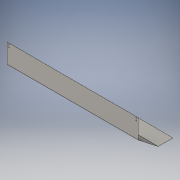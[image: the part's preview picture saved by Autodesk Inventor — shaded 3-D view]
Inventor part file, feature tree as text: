
AUTODESK INVENTOR PART (.ipt)
format: ipt  version: 2016 (Build 200138000, 138)  size: 175,616 bytes
history: native  units: mm
features: sheet_metal_op x7, sketch x4, other x4, hole x1
ambient origin geometry x8: Origin, YZ Plane, XZ Plane, XY Plane, X Axis, Y Axis, Z Axis, Center Point
bodies: Solid1 (feature_tree)
feature tree (16):
  sheet_metal_op  "Face1"
  sheet_metal_op  "Flange1"
  sheet_metal_op  "Flange2"
  hole  "Hole1"  [1 undecoded]
  sketch  "Sketch1"  dims[d0=190.0mm d1=1695.0mm]
  other  "Plate1"
  sketch  "Sketch2"  dims[d2=1.6mm]
  other  "Plate2"
  sheet_metal_op  "Bend1"
  sheet_metal_op  "Corner1"
  sketch  "Sketch3"  dims[d3=1.6mm]
  other  "Plate3"
  sheet_metal_op  "Bend2"
  sheet_metal_op  "Corner2"
  sketch  "Sketch4"  dims[d4=0.8mm d5=3.2mm d6=1.6mm d7=330.0mm d8=6.632251mm d9=1.6mm d10=6.4mm d11=1.6mm d12=1.6mm d13=1.6mm d14=0.8mm d15=3.2mm d16=1.6mm d17=250.0mm d18=9.075712mm d19=1.6mm d20=6.4mm d21=1.6mm d22=1.6mm d23=60.0mm d24=12.0mm d25=12.0mm d26=25.0mm d27=25.0mm d28=15.0mm d29=15.0mm d30=12.0mm d31=12.0mm d32=25.0mm d33=25.0mm d34=12.0mm d35=6.0mm d36=4.0mm d37=2.0mm d38=90.0deg d39=1.6mm d40=20.594885mm d41=15.0mm d42=15.0mm]
  other  "Definition1"
note: 1 required parameter value undecoded (feature->parameter linkage not recoverable at this tier; creation-order binding heuristic only, values carry confidence <= 0.55)
